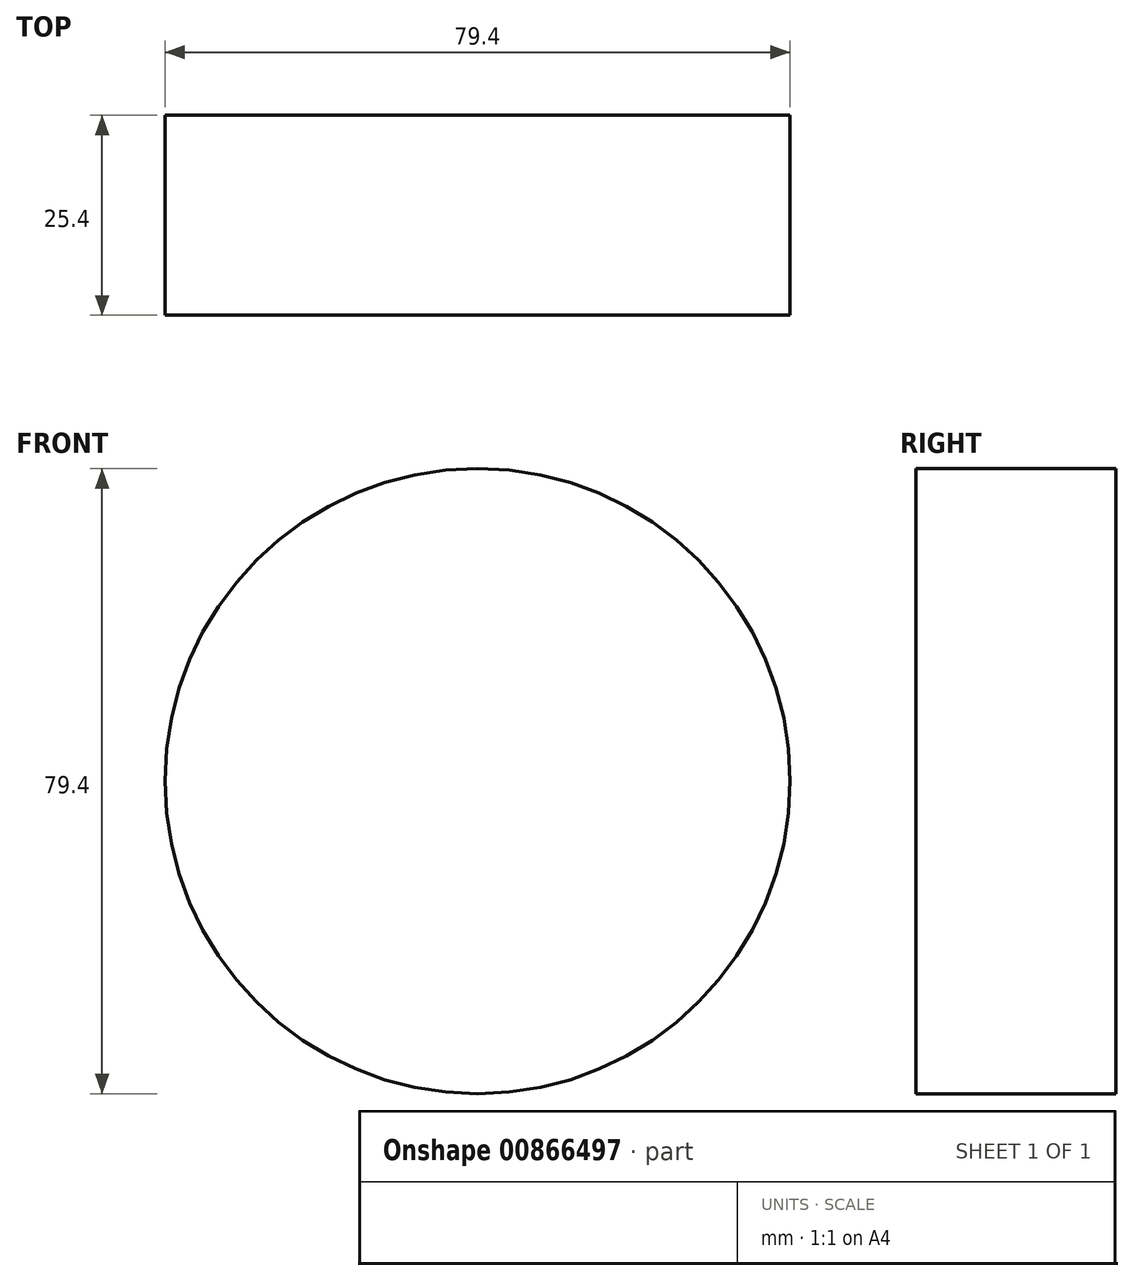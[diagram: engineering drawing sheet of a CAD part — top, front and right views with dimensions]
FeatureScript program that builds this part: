
annotation { "Feature Type Name" : "Feature", "Feature Type Description" : "" }
export const myFeature = defineFeature(function(context is Context, id is Id, definition is map)
    precondition{}
    {
        {
            var Q0;
            Q0=qCreatedBy(makeId("Front.planeOp"),FACE);
            var sketch = newSketch(context, id + "F0", { "sketchPlane" : qUnion([Q0])});
            skCircle(sketch, "E0", {"center": v(0, 0) * mm, "radius": 39.7 * mm});
            skSolve(sketch);
        }
        {
            var Q0;
            Q0=makeQuery(id+"F0.imprint","IMPRINT",FACE,{"disambiguationData":[TD([[makeQuery(id+"F0.imprint","IMPRINT",EDGE,{"derivedFrom":sQuery(id+"F0.wireOp",EDGE,"E0")}),1.0]])]});
            extrude(context, id + "F1", {"entities" : qUnion([Q0]), "depth" : 25.4 * mm, "offsetDistance" : 25.4 * mm});
        }
    });
